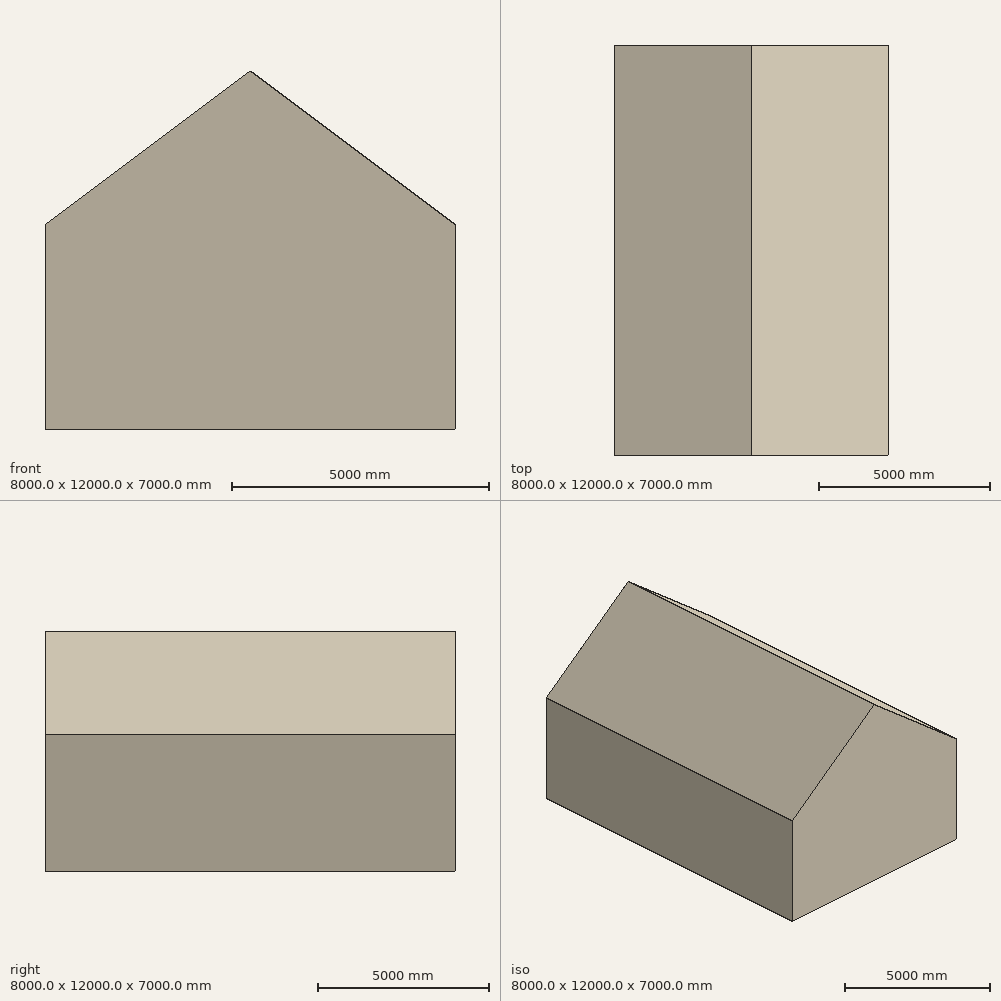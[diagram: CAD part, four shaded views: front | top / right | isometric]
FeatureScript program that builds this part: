
annotation { "Feature Type Name" : "Feature", "Feature Type Description" : "" }
export const myFeature = defineFeature(function(context is Context, id is Id, definition is map)
    precondition{}
    {
        {
            var Q0;
            Q0=qCreatedBy(makeId("Front.planeOp"),FACE);
            var sketch = newSketch(context, id + "F0", { "sketchPlane" : qUnion([Q0])});
            skLineSegment(sketch, "E0.bottom", {"start": v(0, 0) * mm, "end": v(-8000, 0) * mm});
            skLineSegment(sketch, "E0.top", {"start": v(0, 4000) * mm, "end": v(-8000, 4000) * mm});
            skLineSegment(sketch, "E0.left", {"start": v(0, 0) * mm, "end": v(0, 4000) * mm});
            skLineSegment(sketch, "E0.right", {"start": v(-8000, 0) * mm, "end": v(-8000, 4000) * mm});
            skLineSegment(sketch, "E1", {"start": v(-8000, 4000) * mm, "end": v(-4000, 7000) * mm});
            skLineSegment(sketch, "E2", {"start": v(-4000, 7000) * mm, "end": v(0, 4000) * mm});
            skSolve(sketch);
        }
        {
            var Q0;
            Q0=makeQuery(id+"F0.imprint","IMPRINT",FACE,{"disambiguationData":[TD([[makeQuery(id+"F0.imprint","IMPRINT",EDGE,{"derivedFrom":sQuery(id+"F0.wireOp",EDGE,"E0.top")}),-1.0]])]});
            var Q1;
            Q1=makeQuery(id+"F0.imprint","IMPRINT",FACE,{"disambiguationData":[TD([[makeQuery(id+"F0.imprint","IMPRINT",EDGE,{"derivedFrom":sQuery(id+"F0.wireOp",EDGE,"E0.bottom")}),-1.0]])]});
            extrude(context, id + "F1", {"entities" : qUnion([Q0, Q1]), "depth" : 12000 * mm});
        }
    });
